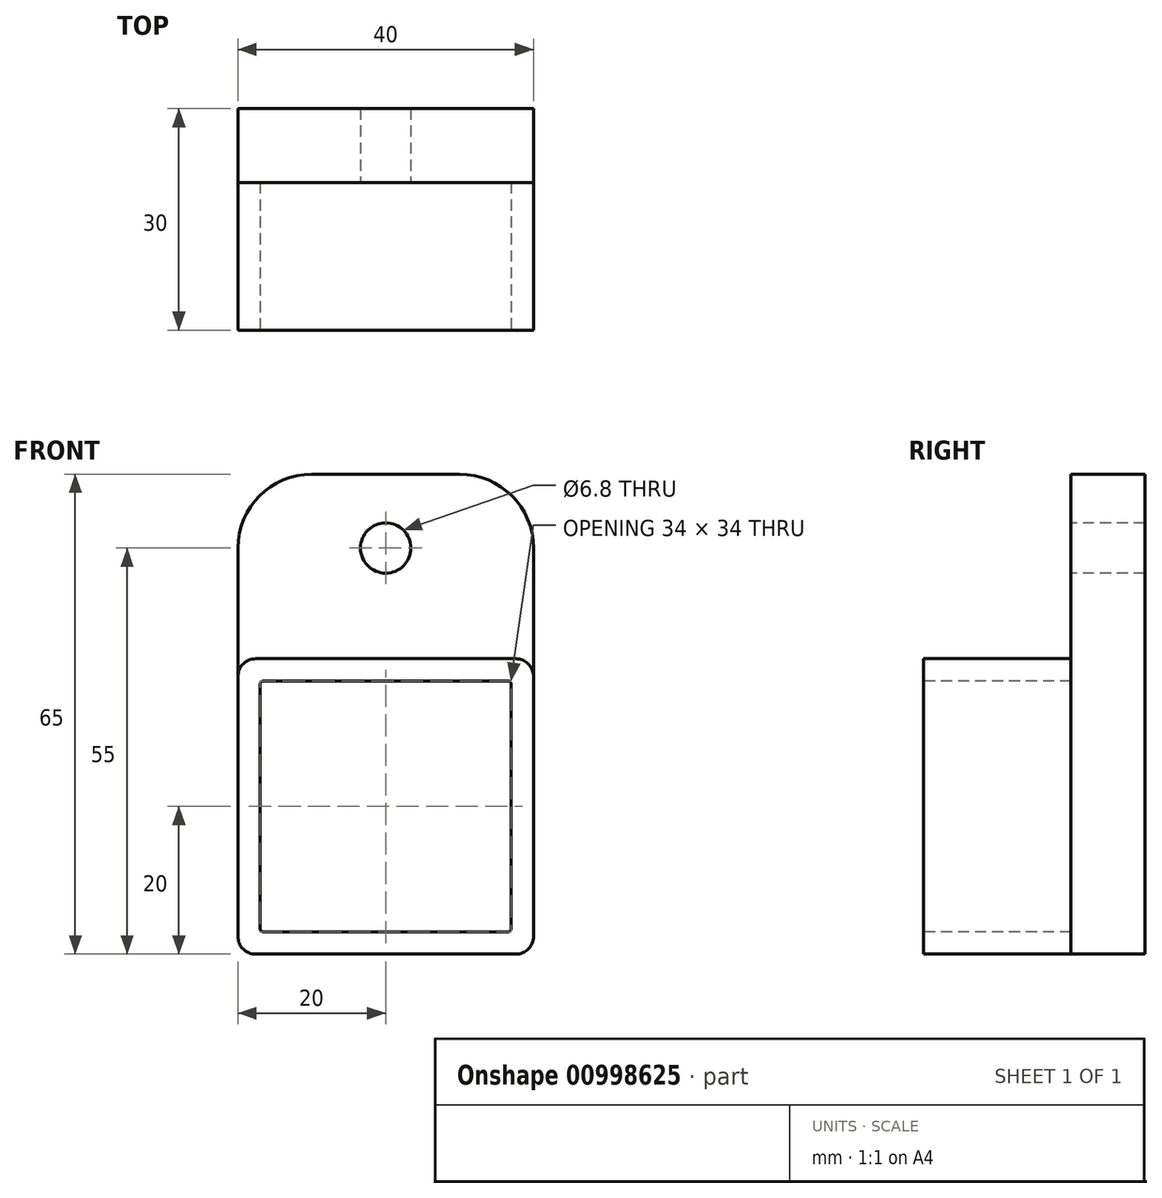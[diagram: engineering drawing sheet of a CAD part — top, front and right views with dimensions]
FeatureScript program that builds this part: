
annotation { "Feature Type Name" : "Feature", "Feature Type Description" : "" }
export const myFeature = defineFeature(function(context is Context, id is Id, definition is map)
    precondition{}
    {
        {
            var Q0;
            Q0=qCreatedBy(makeId("Front.planeOp"),FACE);
            var sketch = newSketch(context, id + "F0", { "sketchPlane" : qUnion([Q0])});
            skLineSegment(sketch, "E0.bottom", {"start": v(-10, 32.5) * mm, "end": v(10, 32.5) * mm});
            skLineSegment(sketch, "E0.top", {"start": v(-20, -32.5) * mm, "end": v(20, -32.5) * mm});
            skLineSegment(sketch, "E0.left", {"start": v(-20, 22.5) * mm, "end": v(-20, -32.5) * mm});
            skLineSegment(sketch, "E0.right", {"start": v(20, 22.5) * mm, "end": v(20, -32.5) * mm});
            skPoint(sketch, "E0.middle", {"position": v(0, 0) * mm});
            skPoint(sketch, "E1.visualSharp", {"position": v(-20, 32.5) * mm});
            skArc(sketch, "E1.filletArc", {"start": v(-10, 32.5) * mm, "mid": v(-17.07, 29.57) * mm, "end": v(-20, 22.5) * mm});
            skPoint(sketch, "E2.visualSharp", {"position": v(20, 32.5) * mm});
            skArc(sketch, "E2.filletArc", {"start": v(20, 22.5) * mm, "mid": v(17.07, 29.57) * mm, "end": v(10, 32.5) * mm});
            skSolve(sketch);
        }
        {
            var Q0;
            Q0=makeQuery(id+"F0.imprint","IMPRINT",FACE,{"disambiguationData":[TD([[makeQuery(id+"F0.imprint","IMPRINT",EDGE,{"derivedFrom":sQuery(id+"F0.wireOp",EDGE,"E0.bottom")}),-1.0]])]});
            extrude(context, id + "F1", {"entities" : qUnion([Q0]), "depth" : 10 * mm, "offsetDistance" : 25 * mm});
        }
        {
            var Q0;
            Q0=makeQuery(id+"F1.opExtrude","CAP_FACE",FACE,{"disambiguationData":[OSD([sQuery(id+"F0.wireOp",EDGE,"E0.bottom"),sQuery(id+"F0.wireOp",EDGE,"E0.top"),sQuery(id+"F0.wireOp",EDGE,"E0.left"),sQuery(id+"F0.wireOp",EDGE,"E0.right"),sQuery(id+"F0.wireOp",EDGE,"E1.filletArc"),sQuery(id+"F0.wireOp",EDGE,"E2.filletArc")])],"isStart":false});
            var sketch = newSketch(context, id + "F2", { "sketchPlane" : qUnion([Q0])});
            skLineSegment(sketch, "E3", {"start": v(-20, -32.5) * mm, "end": v(20, -32.5) * mm});
            skLineSegment(sketch, "E4", {"start": v(20, -32.5) * mm, "end": v(20, 7.5) * mm});
            skLineSegment(sketch, "E5", {"start": v(20, 7.5) * mm, "end": v(-20, 7.5) * mm});
            skLineSegment(sketch, "E6", {"start": v(-20, 7.5) * mm, "end": v(-20, -32.5) * mm});
            skSolve(sketch);
        }
        {
            var Q0;
            Q0=makeQuery(id+"F2.imprint","IMPRINT",FACE,{"disambiguationData":[TD([[makeQuery(id+"F2.imprint","IMPRINT",EDGE,{"derivedFrom":sQuery(id+"F2.wireOp",EDGE,"E3")}),1.0]])]});
            extrude(context, id + "F3", {"entities" : qUnion([Q0]), "depth" : 20 * mm, "offsetDistance" : 25 * mm});
        }
        {
            var Q0;
            Q0=makeQuery(id+"F3.opExtrude","CAP_FACE",FACE,{"disambiguationData":[OSD([sQuery(id+"F2.wireOp",EDGE,"E3"),sQuery(id+"F2.wireOp",EDGE,"E4"),sQuery(id+"F2.wireOp",EDGE,"E5"),sQuery(id+"F2.wireOp",EDGE,"E6")])],"isStart":false});
            var sketch = newSketch(context, id + "F4", { "sketchPlane" : qUnion([Q0])});
            skLineSegment(sketch, "E7.bottom", {"start": v(17, 4.5) * mm, "end": v(-17, 4.5) * mm});
            skLineSegment(sketch, "E7.top", {"start": v(17, -29.5) * mm, "end": v(-17, -29.5) * mm});
            skLineSegment(sketch, "E7.left", {"start": v(17, 4.5) * mm, "end": v(17, -29.5) * mm});
            skLineSegment(sketch, "E7.right", {"start": v(-17, 4.5) * mm, "end": v(-17, -29.5) * mm});
            skPoint(sketch, "E7.middle", {"position": v(0, -12.5) * mm});
            skSolve(sketch);
        }
        {
            var Q0;
            Q0=makeQuery(id+"F4.imprint","IMPRINT",FACE,{"disambiguationData":[TD([[makeQuery(id+"F4.imprint","IMPRINT",EDGE,{"derivedFrom":sQuery(id+"F4.wireOp",EDGE,"E7.bottom")}),1.0]])]});
            var Q1;
            Q1=makeQuery(id+"F3.opExtrude","CAP_FACE",FACE,{"disambiguationData":[OSD([sQuery(id+"F2.wireOp",EDGE,"E3"),sQuery(id+"F2.wireOp",EDGE,"E4"),sQuery(id+"F2.wireOp",EDGE,"E5"),sQuery(id+"F2.wireOp",EDGE,"E6")])],"isStart":true});
            extrude(context, id + "F5", {"entities" : qUnion([Q0]), "operationType" : NewBodyOperationType.REMOVE, "endBound" : BoundingType.UP_TO_SURFACE, "oppositeDirection" : true, "depth" : 25 * mm, "endBoundEntityFace" : qUnion([Q1]), "offsetDistance" : 25 * mm});
        }
        {
            var Q0;
            Q0=makeQuery(id+"F3.opExtrude","SWEPT_EDGE",EDGE,{"disambiguationData":[OSD([sQuery(id+"F0.wireOp",EDGE,"E0.left"),sQuery(id+"F2.wireOp",EDGE,"E5"),sQuery(id+"F2.wireOp",EDGE,"E6")])]});
            var Q1;
            Q1=makeQuery(id+"F3.opExtrude","SWEPT_EDGE",EDGE,{"disambiguationData":[OSD([sQuery(id+"F0.wireOp",EDGE,"E0.right"),sQuery(id+"F2.wireOp",EDGE,"E4"),sQuery(id+"F2.wireOp",EDGE,"E5")])]});
            var Q2;
            Q2=makeQuery(id+"F3.opExtrude","SWEPT_EDGE",EDGE,{"disambiguationData":[OSD([sQuery(id+"F2.wireOp",EDGE,"E3"),sQuery(id+"F2.wireOp",EDGE,"E6")])]});
            var Q3;
            Q3=makeQuery(id+"F3.opExtrude","SWEPT_EDGE",EDGE,{"disambiguationData":[OSD([sQuery(id+"F2.wireOp",EDGE,"E3"),sQuery(id+"F2.wireOp",EDGE,"E4")])]});
            fillet(context, id + "F6", {"entities" : qUnion([Q0, Q1, Q2, Q3]), "radius" : 2.4 * mm, "tangentPropagation" : true, "allowEdgeOverflow" : false});
        }
        {
            var Q0;
            Q0=makeQuery(id+"F5.boolean.opBoolean","COPY",EDGE,{"derivedFrom":makeQuery(id+"F5.opExtrude","SWEPT_EDGE",EDGE,{"disambiguationData":[OSD([sQuery(id+"F4.wireOp",EDGE,"E7.top"),sQuery(id+"F4.wireOp",EDGE,"E7.right")])]})});
            var Q1;
            Q1=makeQuery(id+"F5.boolean.opBoolean","COPY",EDGE,{"derivedFrom":makeQuery(id+"F5.opExtrude","SWEPT_EDGE",EDGE,{"disambiguationData":[OSD([sQuery(id+"F4.wireOp",EDGE,"E7.bottom"),sQuery(id+"F4.wireOp",EDGE,"E7.right")])]})});
            var Q2;
            Q2=makeQuery(id+"F5.boolean.opBoolean","COPY",EDGE,{"derivedFrom":makeQuery(id+"F5.opExtrude","SWEPT_EDGE",EDGE,{"disambiguationData":[OSD([sQuery(id+"F4.wireOp",EDGE,"E7.bottom"),sQuery(id+"F4.wireOp",EDGE,"E7.left")])]})});
            var Q3;
            Q3=makeQuery(id+"F5.boolean.opBoolean","COPY",EDGE,{"derivedFrom":makeQuery(id+"F5.opExtrude","SWEPT_EDGE",EDGE,{"disambiguationData":[OSD([sQuery(id+"F4.wireOp",EDGE,"E7.top"),sQuery(id+"F4.wireOp",EDGE,"E7.left")])]})});
            fillet(context, id + "F7", {"entities" : qUnion([Q0, Q1, Q2, Q3]), "radius" : .5 * mm, "tangentPropagation" : true, "allowEdgeOverflow" : false});
        }
        {
            var Q0;
            Q0=makeQuery(id+"F1.opExtrude","SWEPT_EDGE",EDGE,{"disambiguationData":[OSD([sQuery(id+"F0.wireOp",EDGE,"E0.top"),sQuery(id+"F0.wireOp",EDGE,"E0.left")])]});
            var Q1;
            Q1=makeQuery(id+"F1.opExtrude","SWEPT_EDGE",EDGE,{"disambiguationData":[OSD([sQuery(id+"F0.wireOp",EDGE,"E0.top"),sQuery(id+"F0.wireOp",EDGE,"E0.right")])]});
            fillet(context, id + "F8", {"entities" : qUnion([Q0, Q1]), "radius" : 2.4 * mm, "tangentPropagation" : true, "allowEdgeOverflow" : false});
        }
        {
            var Q0;
            Q0=makeQuery(id+"F1.opExtrude","CAP_FACE",FACE,{"disambiguationData":[OSD([sQuery(id+"F0.wireOp",EDGE,"E0.bottom"),sQuery(id+"F0.wireOp",EDGE,"E0.top"),sQuery(id+"F0.wireOp",EDGE,"E0.left"),sQuery(id+"F0.wireOp",EDGE,"E0.right"),sQuery(id+"F0.wireOp",EDGE,"E1.filletArc"),sQuery(id+"F0.wireOp",EDGE,"E2.filletArc")])],"isStart":false});
            var sketch = newSketch(context, id + "F9", { "sketchPlane" : qUnion([Q0])});
            skPoint(sketch, "E8", {"position": v(0, 22.5) * mm});
            skSolve(sketch);
        }
        {
            var Q0;
            Q0=sQuery(id+"F9.wireOp",VERTEX,"E8");
            var Q1;
            Q1=makeQuery(id+"F1.opExtrude","SWEPT_BODY",BODY,{"disambiguationData":[OSD([sQuery(id+"F0.wireOp",EDGE,"E0.bottom"),sQuery(id+"F0.wireOp",EDGE,"E0.top"),sQuery(id+"F0.wireOp",EDGE,"E0.left"),sQuery(id+"F0.wireOp",EDGE,"E0.right"),sQuery(id+"F0.wireOp",EDGE,"E1.filletArc"),sQuery(id+"F0.wireOp",EDGE,"E2.filletArc")])]});
            hole(context, id + "F10", {"style" : HoleStyle.SIMPLE, "endStyle" : HoleEndStyle.THROUGH, "standardTappedOrClearance" : lookupTablePath({ "standard" : "ISO", "engagement" : "75%", "pitch" : "1.25 mm", "size" : "M8", "type" : "Tapped" }), "standardBlindInLast" : lookupTablePath({ "standard" : "ISO", "fit" : "Normal", "engagement" : "75%", "pitch" : "1.25 mm", "size" : "M8", "type" : "Clearance & tapped" }), "holeDiameter" : 6.8 * mm, "majorDiameter" : 8 * mm, "showTappedDepth" : true, "isTappedThrough" : true, "tappedDepth" : 12 * mm, "tapClearance" : 3, "locations" : qUnion([Q0]), "scope" : qUnion([Q1])});
        }
    });
